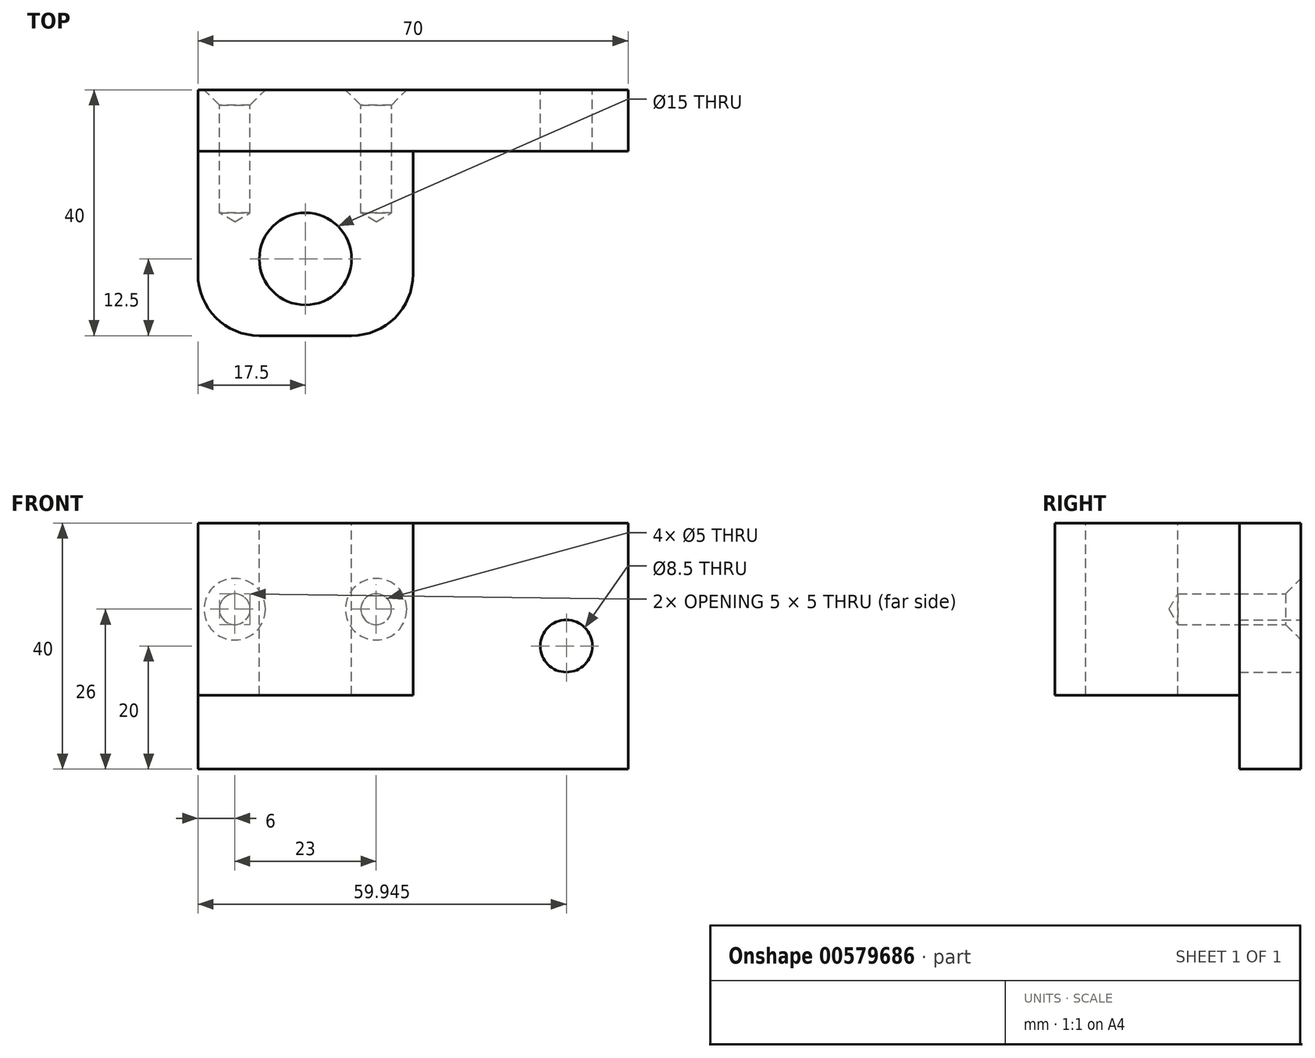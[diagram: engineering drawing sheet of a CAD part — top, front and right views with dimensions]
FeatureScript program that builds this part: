
annotation { "Feature Type Name" : "Feature", "Feature Type Description" : "" }
export const myFeature = defineFeature(function(context is Context, id is Id, definition is map)
    precondition{}
    {
        {
            var Q0;
            Q0=qCreatedBy(makeId("Front.planeOp"),FACE);
            var sketch = newSketch(context, id + "F0", { "sketchPlane" : qUnion([Q0])});
            skLineSegment(sketch, "E0.bottom", {"start": v(0, 0) * mm, "end": v(70, 0) * mm});
            skLineSegment(sketch, "E0.top", {"start": v(0, 40) * mm, "end": v(70, 40) * mm});
            skLineSegment(sketch, "E0.left", {"start": v(0, 0) * mm, "end": v(0, 40) * mm});
            skLineSegment(sketch, "E0.right", {"start": v(70, 0) * mm, "end": v(70, 40) * mm});
            skCircle(sketch, "E1", {"center": v(59.95, 20) * mm, "radius": 4.25 * mm});
            skPoint(sketch, "E1.centerSnap0", {"position": v(0, 20) * mm});
            skSolve(sketch);
        }
        {
            var Q0;
            Q0=makeQuery(id+"F0.imprint","IMPRINT",FACE,{"disambiguationData":[TD([[makeQuery(id+"F0.imprint","IMPRINT",EDGE,{"derivedFrom":sQuery(id+"F0.wireOp",EDGE,"E0.bottom")}),1.0]])]});
            extrude(context, id + "F1", {"entities" : qUnion([Q0]), "depth" : 10 * mm, "offsetDistance" : 25 * mm});
        }
        {
            var Q0;
            Q0=makeQuery(id+"F1.opExtrude","CAP_FACE",FACE,{"disambiguationData":[OSD([sQuery(id+"F0.wireOp",EDGE,"E0.bottom"),sQuery(id+"F0.wireOp",EDGE,"E0.top"),sQuery(id+"F0.wireOp",EDGE,"E0.left"),sQuery(id+"F0.wireOp",EDGE,"E0.right"),sQuery(id+"F0.wireOp",EDGE,"E1")])],"isStart":false});
            var sketch = newSketch(context, id + "F2", { "sketchPlane" : qUnion([Q0])});
            skLineSegment(sketch, "E2.bottom", {"start": v(0, 40) * mm, "end": v(35, 40) * mm});
            skLineSegment(sketch, "E2.top", {"start": v(0, 12) * mm, "end": v(35, 12) * mm});
            skLineSegment(sketch, "E2.left", {"start": v(0, 40) * mm, "end": v(0, 12) * mm});
            skLineSegment(sketch, "E2.right", {"start": v(35, 40) * mm, "end": v(35, 12) * mm});
            skCircle(sketch, "E3", {"center": v(5, 26) * mm, "radius": 2.5 * mm});
            skPoint(sketch, "E3.centerSnap0", {"position": v(0, 26) * mm});
            skCircle(sketch, "E4", {"center": v(30, 26) * mm, "radius": 2.5 * mm});
            skSolve(sketch);
        }
        {
            var Q0;
            Q0=makeQuery(id+"F2.imprint","IMPRINT",FACE,{"disambiguationData":[TD([[makeQuery(id+"F2.imprint","IMPRINT",EDGE,{"derivedFrom":sQuery(id+"F2.wireOp",EDGE,"E2.bottom")}),-1.0]])]});
            var Q1;
            Q1=makeQuery(id+"F2.imprint","IMPRINT",FACE,{"disambiguationData":[TD([[makeQuery(id+"F2.imprint","IMPRINT",EDGE,{"derivedFrom":sQuery(id+"F2.wireOp",EDGE,"E3")}),1.0]])]});
            var Q2;
            Q2=makeQuery(id+"F2.imprint","IMPRINT",FACE,{"disambiguationData":[TD([[makeQuery(id+"F2.imprint","IMPRINT",EDGE,{"derivedFrom":sQuery(id+"F2.wireOp",EDGE,"E4")}),1.0]])]});
            extrude(context, id + "F3", {"entities" : qUnion([Q0, Q1, Q2]), "depth" : 30 * mm, "offsetDistance" : 25 * mm});
        }
        {
            var Q0;
            Q0=makeQuery(id+"F3.opExtrude","SWEPT_FACE",FACE,{"disambiguationData":[OSD([sQuery(id+"F2.wireOp",EDGE,"E2.bottom")])]});
            var sketch = newSketch(context, id + "F4", { "sketchPlane" : qUnion([Q0])});
            skCircle(sketch, "E5", {"center": v(17.5, -27.5) * mm, "radius": 7.5 * mm});
            skPoint(sketch, "E5.centerSnap0", {"position": v(17.5, -10) * mm});
            skPoint(sketch, "E5.centerSnap1", {"position": v(0, -25) * mm});
            skSolve(sketch);
        }
        {
            var Q0;
            Q0=makeQuery(id+"F4.imprint","IMPRINT",FACE,{"disambiguationData":[TD([[makeQuery(id+"F4.imprint","IMPRINT",EDGE,{"derivedFrom":sQuery(id+"F4.wireOp",EDGE,"E5")}),1.0]])]});
            extrude(context, id + "F5", {"entities" : qUnion([Q0]), "operationType" : NewBodyOperationType.REMOVE, "endBound" : BoundingType.THROUGH_ALL, "oppositeDirection" : true, "depth" : 25 * mm, "offsetDistance" : 25 * mm});
        }
        {
            var Q0;
            Q0=makeQuery(id+"F1.opExtrude","CAP_FACE",FACE,{"disambiguationData":[OSD([sQuery(id+"F0.wireOp",EDGE,"E0.bottom"),sQuery(id+"F0.wireOp",EDGE,"E0.top"),sQuery(id+"F0.wireOp",EDGE,"E0.left"),sQuery(id+"F0.wireOp",EDGE,"E0.right"),sQuery(id+"F0.wireOp",EDGE,"E1")])],"isStart":true});
            var sketch = newSketch(context, id + "F6", { "sketchPlane" : qUnion([Q0])});
            skLineSegment(sketch, "E6.bottom", {"start": v(-35, 40) * mm, "end": v(0, 40) * mm});
            skLineSegment(sketch, "E6.top", {"start": v(-35, 12) * mm, "end": v(0, 12) * mm});
            skLineSegment(sketch, "E6.left", {"start": v(-35, 40) * mm, "end": v(-35, 12) * mm});
            skLineSegment(sketch, "E6.right", {"start": v(0, 40) * mm, "end": v(0, 12) * mm});
            skCircle(sketch, "E7", {"center": v(-29, 26) * mm, "radius": 2.5 * mm});
            skPoint(sketch, "E7.centerSnap0", {"position": v(-35, 26) * mm});
            skCircle(sketch, "E8", {"center": v(-6, 26) * mm, "radius": 2.5 * mm});
            skSolve(sketch);
        }
        {
            var Q0;
            Q0=sQuery(id+"F6.wireOp",VERTEX,"E7.center");
            var Q1;
            Q1=sQuery(id+"F6.wireOp",VERTEX,"E8.center");
            var Q2;
            Q2=makeQuery(id+"F3.opExtrude","SWEPT_BODY",BODY,{"disambiguationData":[OSD([sQuery(id+"F2.wireOp",EDGE,"E2.bottom"),sQuery(id+"F2.wireOp",EDGE,"E2.top"),sQuery(id+"F2.wireOp",EDGE,"E2.left"),sQuery(id+"F2.wireOp",EDGE,"E2.right")])]});
            var Q3;
            Q3=makeQuery(id+"F1.opExtrude","SWEPT_BODY",BODY,{"disambiguationData":[OSD([sQuery(id+"F0.wireOp",EDGE,"E0.bottom"),sQuery(id+"F0.wireOp",EDGE,"E0.top"),sQuery(id+"F0.wireOp",EDGE,"E0.left"),sQuery(id+"F0.wireOp",EDGE,"E0.right"),sQuery(id+"F0.wireOp",EDGE,"E1")])]});
            hole(context, id + "F7", {"style" : HoleStyle.C_SINK, "endStyle" : HoleEndStyle.BLIND, "holeDiameter" : 5 * mm, "cSinkDiameter" : 10 * mm, "cSinkAngle" : 90 * degree, "majorDiameter" : 5 * mm, "holeDepth" : 20 * mm, "isTappedThrough" : true, "tappedDepth" : 12 * mm, "tapClearance" : 3, "locations" : qUnion([Q0, Q1]), "scope" : qUnion([Q2, Q3])});
        }
        {
            var Q0;
            Q0=makeQuery(id+"F3.opExtrude","CAP_EDGE",EDGE,{"disambiguationData":[OSD([sQuery(id+"F2.wireOp",EDGE,"E2.right")])],"isStart":false});
            var Q1;
            Q1=makeQuery(id+"F3.opExtrude","CAP_EDGE",EDGE,{"disambiguationData":[OSD([sQuery(id+"F2.wireOp",EDGE,"E2.left")])],"isStart":false});
            fillet(context, id + "F8", {"entities" : qUnion([Q0, Q1]), "radius" : 10 * mm, "tangentPropagation" : true, "allowEdgeOverflow" : false});
        }
    });
